# Revit family: ledroad-st-p2_re489-80w-dali-730_705000067900
name_source: partatom
category: Lighting Fixtures
units: mm (PartAtom-declared; Revit-internal decimal feet)

## family parameters
Cut with Voids When Loaded = No
Host = Face
Light Source = No
Part Type = Normal
Room Calculation Point = No
Round Connector Dimension = Use Diameter
Shared = No

## types (1)
- LEDRoad-St-P2 Re489-80W-DALI-730 (1 x LED, 12000 lm, 3000)
    Apparent Load = 80 VA
    Approval mark = CE, ENEC
    CIE Flux Codes = 46 81 99 100 100
    Color Rendering = 70
    Color Temperature = 3000
    Control Gear = Electronic ballast
    Default Elevation = 1800 mm
    Description = Easy installation and maintenance via openable driver compartment . Flexible and adjustable pole connector (60mm & 76mm) for both side entry and pole top mounting (order separately).
    Frequency = 60 Hz
    Height = 116 mm
    Lamp = 1 x LED
    Lamp Light Flux = 12000 lm
    Lamp count = 1
    Length = 489 mm
    Luminous efficacy = 150 lm/W
    Manufacturer = OPPLE
    ModVariant = No
    Model = 705000067900
    Mounting Place = Pole
    Mounting Type = Pole annexe
    Number of Poles = 1
    OnlyDefault = Yes
    Power Factor = 1
    Product Name = LEDRoad-St-P2 Re489-80W-DALI-730
    Product group = Street luminaire
    ProductGroupID = 15
    Protection Class = Protection class II
    Protection Degree = IP 66
    RLX_Detail_Level = 1
    RlxData = <blob elided: 198449 chars, md5=a96a1b14>
    Socket = socket
    Standby Power = 0 W
    System Light Flux = 12000 lm
    System Power = 80 W
    Type Comments = Product without accessories
    Type Image = stratus_v2.jpg
    URL = http://relux.com
    VarID = ---
    Voltage = 230 V
    Voltage Range = 220-240 V
    Weight = 0.00 kg
    Width = 255 mm

## geometry (parser evidence)
native form markers: Blend x4, Sweep x8
no freeform markers — native parametric forms only
